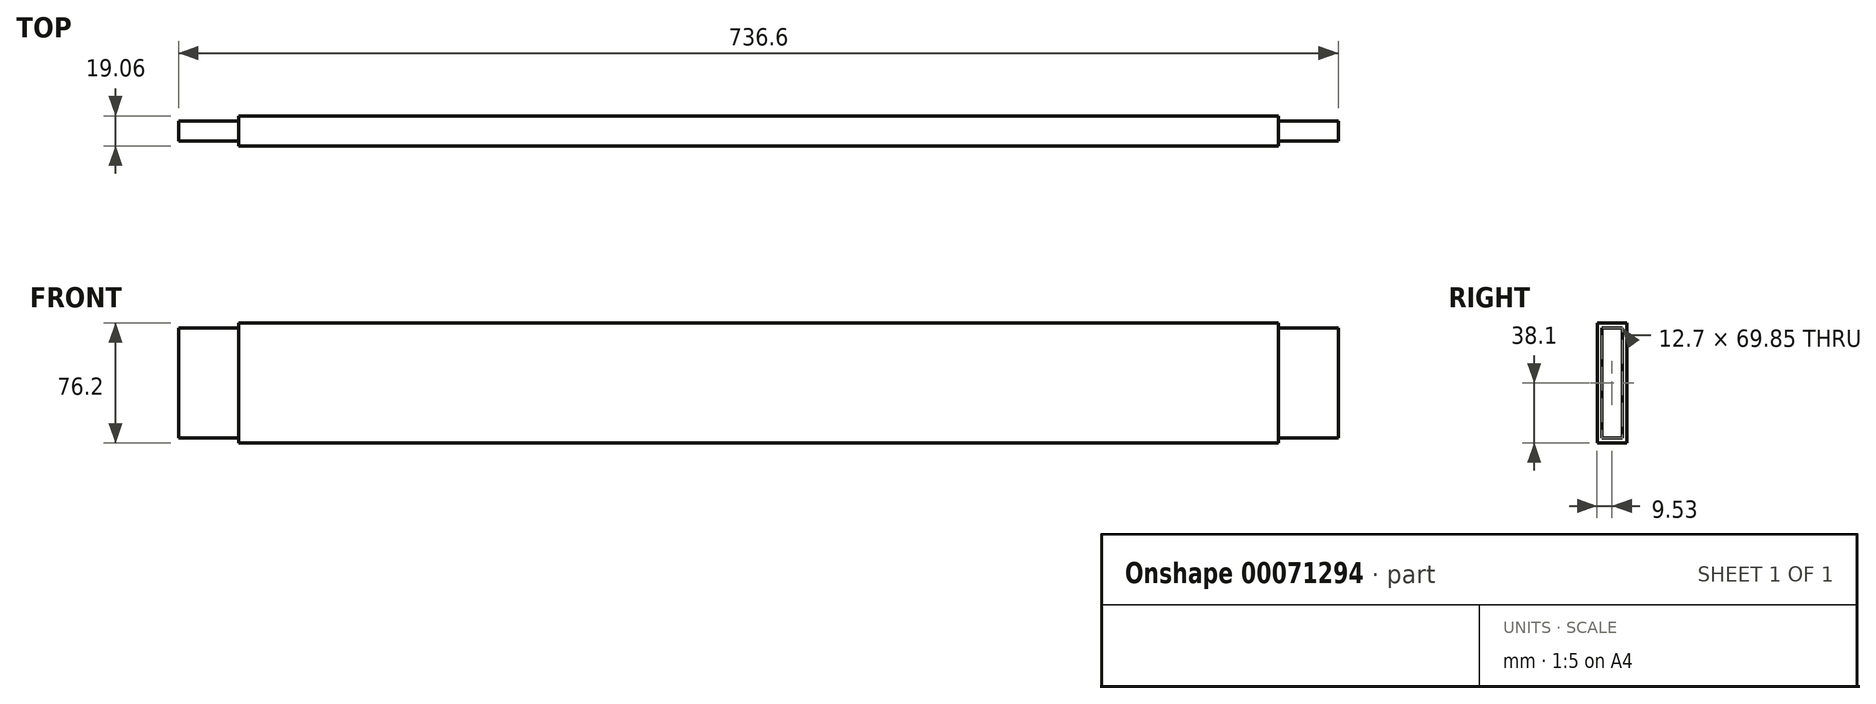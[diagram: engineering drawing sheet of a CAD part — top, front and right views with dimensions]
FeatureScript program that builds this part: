
annotation { "Feature Type Name" : "Feature", "Feature Type Description" : "" }
export const myFeature = defineFeature(function(context is Context, id is Id, definition is map)
    precondition{}
    {
        {
            var Q0;
            Q0=qCreatedBy(makeId("Front.planeOp"),FACE);
            var sketch = newSketch(context, id + "F0", { "sketchPlane" : qUnion([Q0])});
            skLineSegment(sketch, "E0.bottom", {"start": v(-330.2, 38.1) * mm, "end": v(330.2, 38.1) * mm});
            skLineSegment(sketch, "E0.top", {"start": v(-330.2, -38.1) * mm, "end": v(330.2, -38.1) * mm});
            skLineSegment(sketch, "E0.left", {"start": v(-330.2, 38.1) * mm, "end": v(-330.2, -38.1) * mm});
            skLineSegment(sketch, "E0.right", {"start": v(330.2, 38.1) * mm, "end": v(330.2, -38.1) * mm});
            skSolve(sketch);
        }
        {
            var Q0;
            Q0=makeQuery(id+"F0.imprint","IMPRINT",FACE,{"disambiguationData":[TD([[makeQuery(id+"F0.imprint","IMPRINT",EDGE,{"derivedFrom":sQuery(id+"F0.wireOp",EDGE,"E0.bottom")}),-1.0]])]});
            extrude(context, id + "F1", {"entities" : qUnion([Q0]), "endBound" : BoundingType.SYMMETRIC, "depth" : 19.05 * mm});
        }
        {
            var Q0;
            Q0=makeQuery(id+"F1.opExtrude","SWEPT_FACE",FACE,{"disambiguationData":[OSD([sQuery(id+"F0.wireOp",EDGE,"E0.right")])]});
            var sketch = newSketch(context, id + "F2", { "sketchPlane" : qUnion([Q0])});
            skLineSegment(sketch, "E1.bottom", {"start": v(-6.35, 34.92) * mm, "end": v(6.35, 34.92) * mm});
            skLineSegment(sketch, "E1.top", {"start": v(-6.35, -34.93) * mm, "end": v(6.35, -34.93) * mm});
            skLineSegment(sketch, "E1.left", {"start": v(-6.35, 34.92) * mm, "end": v(-6.35, -34.93) * mm});
            skLineSegment(sketch, "E1.right", {"start": v(6.35, 34.92) * mm, "end": v(6.35, -34.93) * mm});
            skSolve(sketch);
        }
        {
            var Q0;
            Q0=makeQuery(id+"F1.opExtrude","SWEPT_FACE",FACE,{"disambiguationData":[OSD([sQuery(id+"F0.wireOp",EDGE,"E0.left")])]});
            var sketch = newSketch(context, id + "F3", { "sketchPlane" : qUnion([Q0])});
            skLineSegment(sketch, "E2.bottom", {"start": v(-6.35, 34.93) * mm, "end": v(6.35, 34.93) * mm});
            skLineSegment(sketch, "E2.top", {"start": v(-6.35, -34.93) * mm, "end": v(6.35, -34.93) * mm});
            skLineSegment(sketch, "E2.left", {"start": v(-6.35, 34.93) * mm, "end": v(-6.35, -34.93) * mm});
            skLineSegment(sketch, "E2.right", {"start": v(6.35, 34.93) * mm, "end": v(6.35, -34.93) * mm});
            skSolve(sketch);
        }
        {
            var Q0;
            Q0=qSketchRegion(id+"F2",true);
            var Q1;
            Q1=makeQuery(id+"F3.imprint","IMPRINT",FACE,{"disambiguationData":[TD([[makeQuery(id+"F3.imprint","IMPRINT",EDGE,{"derivedFrom":sQuery(id+"F3.wireOp",EDGE,"E2.bottom")}),-1.0]])]});
            extrude(context, id + "F4", {"entities" : qUnion([Q0, Q1]), "operationType" : NewBodyOperationType.ADD, "depth" : 38.1 * mm});
        }
        {
            var Q0;
            Q0=makeQuery(id+"F3.imprint","IMPRINT",FACE,{"disambiguationData":[TD([[makeQuery(id+"F3.imprint","IMPRINT",EDGE,{"derivedFrom":sQuery(id+"F3.wireOp",EDGE,"E2.bottom")}),-1.0]])]});
            extrude(context, id + "F5", {"entities" : qUnion([Q0]), "operationType" : NewBodyOperationType.ADD, "depth" : 38.1 * mm});
        }
    });
